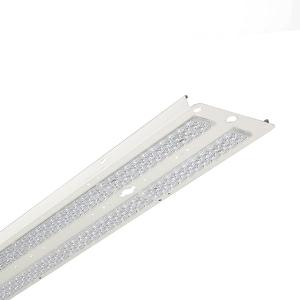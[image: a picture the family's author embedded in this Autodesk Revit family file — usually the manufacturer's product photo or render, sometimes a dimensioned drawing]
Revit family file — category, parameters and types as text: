
# Revit family: 3f_filippi_-_kit_led_retrofit_per_schermo_in_vetro_3f_filippi_-_a5210_-_kit_led_i3f_76_a3f_91_-_l1565_-__b391402b403b61e2
name_source: partatom
category: Lighting Fixtures
units: mm (PartAtom-declared; Revit-internal decimal feet)

## family parameters
Cut with Voids When Loaded = No
Host = Face
Light Source = No
Part Type = Normal
Room Calculation Point = No
Round Connector Dimension = Use Diameter
Shared = No

## types (1)
- 3F Filippi - Kit LED Retrofit per schermo in vetro (1 x LED, 11397 lm, 74 W, 4000 K)
    Apparent Load = 74 VA
    Approval mark = ENEC
    CIE Flux Codes = 64 96 100 100 100
    Color Rendering = 80
    Color Temperature = 4000 K
    Control Gear = Electronic ballast
    Default Elevation = 1800 mm
    Description = Led retrofit kit suitable for Fluorescent Beta 2x i3F 76 and A3F 91 luminaires.

ILLUMINOTECHNICAL
Luminous efficiency 100% (DLOR 100%, ULOR 0%).
Initial luminous flux of the luminaire 11397 lm.
Wide symmetric distribution.
Installation Interdistance Transv.D = 1.45 x hu - Long.D = 1.63 x hu.
Tabular UGR (CIE 117 - 4H-8H; S=0.25H; 70/50/20): RUG 19.3 - 20.9.
Beam angle: 97° - 102°.
Luminous efficacy 154 lm/W.
Lifetime (L93/B10): 30000 h. (tq+25°C)
Lifetime (L90/B10): 50000 h. (tq+25°C)
Lifetime (L85/B10): 80000 h. (tq+25°C)
Lifetime (L80/B10): 100000 h. (tq+25°C)
Lifetime (L85/B10): 50000 h. (tq+40°C)
Sudden decreased luminous flux after 50000 hours: 0% (C0).
Photobiological safety in compliance with IEC/TR 62778: RG0 risk exempt, (IEC 62471).
In compliance with IEC/EN 62722-2-1 - IEC/EN 62717 standards.

SOURCE
2 linear LED modules 40W/840.
Energy efficiency class (UE 2019/2020 - UE 2019/2015): C.
CIE 13.3 Colour rendering index: CRI >80 (R9 <50%).
IES TM-30 Fidelity Index: Rf = 84 Rg = 95.
CCT nominal colour temperature 4000 K.
Colour initial tolerance (MacAdam): SDCM 3.

MECHANICAL
Gear-tray unit in hot-galvanised steel, painted in white polyester, fixed to the housing by means of "Ribloc" rapid devices in galvanised steel, hinged opening.
Lenses for wide distribution, in transparent methacrylate (PMMA) with external flat surface.
Luminaire with limited surface temperature. - D - (EN 60598-2-24)
Dimensions: 1565x235 mm, height 105 mm. Weight 3.6 kg.
Glow-wire test resistance 850°C.

ELECTRICAL
Halogen Free electronic wiring 230V-50/60Hz, power factor 0.95, THD <25%, constant output current, class I, 1 driver.
Power of the luminaire 74 W.
CE - IEC 60598-1 - EN 60598-1.
SAFE FLICKER: PstLM=<1 and SVM=<0.4 (IEC TR 61547-1 and IEC TR 63158), to ensure a more comfortable and safe light.
Luminaire compliant with EN 60598-2-22 for power supply from a centralised emergency system CPSS (Central Power Supply System), not incorporated in the luminaire - high risk areas excluded. The default power and flux are 100% in AC and 100% in DC.
Ambient temperature from -20°C to +40°C.
Temperature class T6 max 85°C.
Relative humidity UR: <85%.

INSTALLATION
Retrofit.
Correct installation of the retrofit LED kit, compliant with EN 60598-1 and CE marked, inside the 3F Filippi - Beta 2x i3F 76 and A3F 91 Fluorescent luminaires must be only carried out by qualified personnel to ensure compliance with the national installation standards.
Attention: to maintain the degree of protection of the device and for the purposes of validity of the guarantee of the new retrofit kits, it is imperative to replace the old cable guides (on the body of the device) with the new ones supplied.
All accessories dedicated to this product are available on the Catalog and on our website www.3F-Filippi.com.

WARNING
Fixture not suitable for cold stores with an ambient temperature <0°C and/or relative humidity >85%.
Luminaire designed for disposal/recycling at end-of-life.
Replaceable (LED only) light source by a professional. Replaceable control gear by a professional.
    Height = 105 mm
    Lamp = 1 x LED
    Lamp Light Flux = 11397 lm
    Lamp Power = 74 W
    Lamp count = 1
    Length = 1565 mm
    Lifetime = 50000 h
    Luminous efficacy = 154 lm/W
    Manufacturer = 3F Filippi
    ModVariant = No
    Model = 3F Filippi - A5210 - Kit LED i3F 76,A3F 91 - L1565 - L 2x40W AMPIO
    Mounting Place = Ceiling
    Mounting Type = Surface mounted
    Number of Poles = 1
    OnlyDefault = Yes
    Power Factor = 1
    Product Name = 3F Filippi - Kit LED Retrofit per schermo in vetro
    Product group = ceiling mounted luminaire
    ProductGroupID = 3
    Protection Class = Protection class I
    Protection Degree = Degree of protection
    RLX_Detail_Level = 1
    RLX_Emergency_Light_Flux = 0 lm
    RLX_Emergency_Type = 0
    RLX_Emergency_Type_DB = No
    RlxData = <blob elided: 66973 chars, md5=55046fe5>
    Socket = socket
    Standby Power = 0 W
    System Light Flux = 11397 lm
    System Power = 74 W
    Type Comments = Product without accessories
    Type Image = 3ffilippi_a5210.jpg
    URL = http://relux.com
    VarID = ---
    Voltage = 0 V
    Weight = 0.00 kg
    Width = 235 mm

## geometry (parser evidence)
native form markers: Blend x4, Sweep x10
no freeform markers — native parametric forms only
